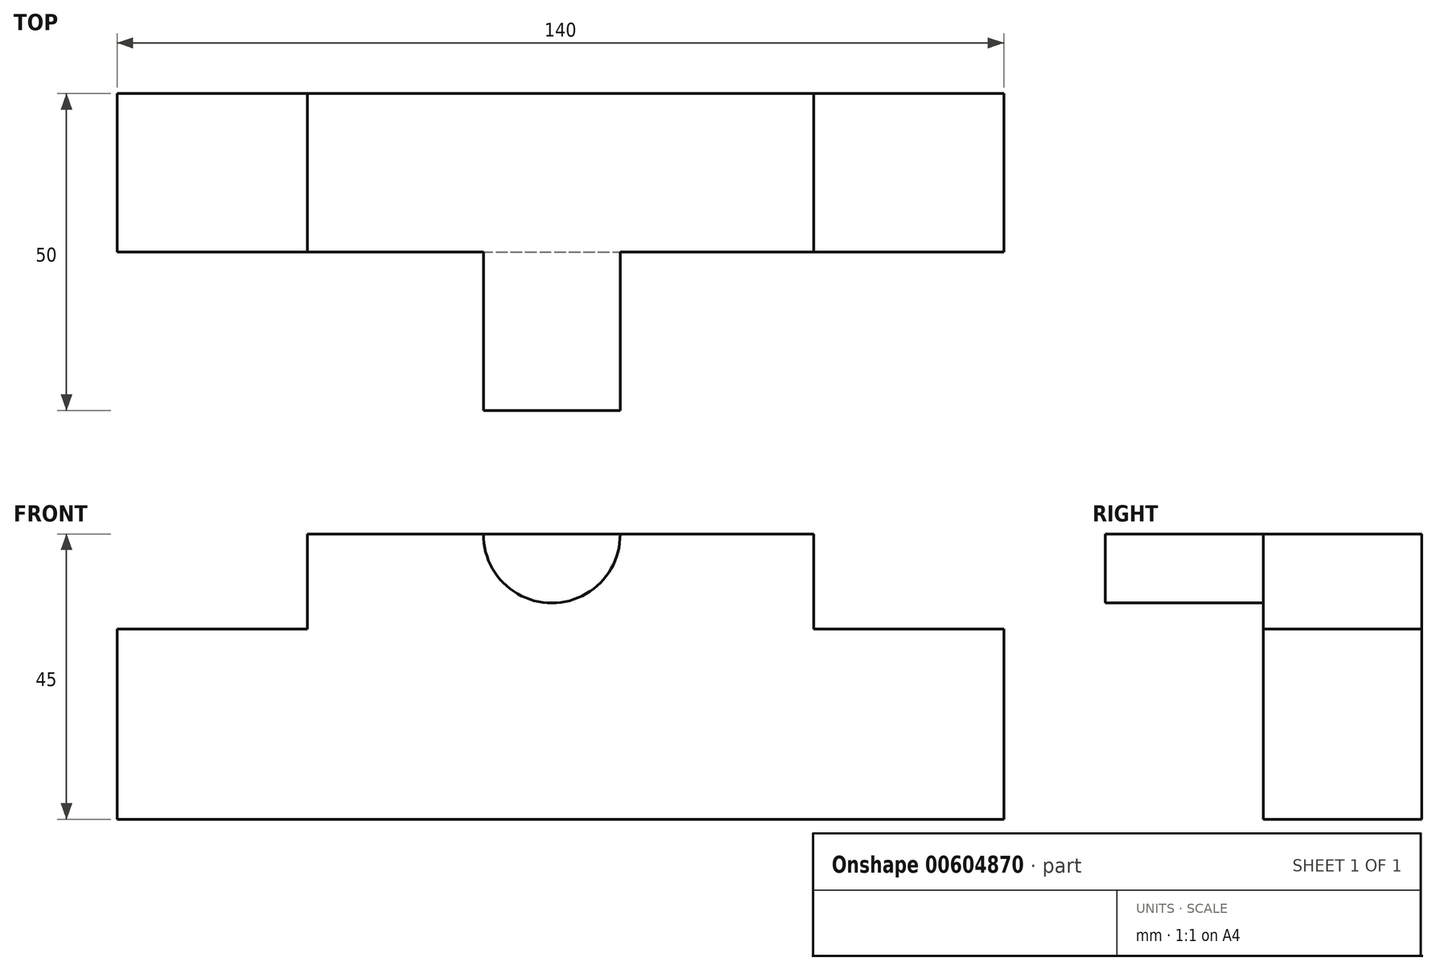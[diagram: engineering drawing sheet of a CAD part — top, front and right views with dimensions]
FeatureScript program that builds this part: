
annotation { "Feature Type Name" : "Feature", "Feature Type Description" : "" }
export const myFeature = defineFeature(function(context is Context, id is Id, definition is map)
    precondition{}
    {
        {
            var Q0;
            Q0=qCreatedBy(makeId("Front.planeOp"),FACE);
            var sketch = newSketch(context, id + "F0", { "sketchPlane" : qUnion([Q0])});
            skLineSegment(sketch, "E0", {"start": v(-68.52, 0) * mm, "end": v(71.48, 0) * mm});
            skLineSegment(sketch, "E1", {"start": v(-68.52, 0) * mm, "end": v(-68.52, 30) * mm});
            skLineSegment(sketch, "E2", {"start": v(71.48, 0) * mm, "end": v(71.48, 30) * mm});
            skLineSegment(sketch, "E3", {"start": v(-68.52, 30) * mm, "end": v(-38.52, 30) * mm});
            skLineSegment(sketch, "E4", {"start": v(71.48, 30) * mm, "end": v(41.48, 30) * mm});
            skLineSegment(sketch, "E5", {"start": v(-38.52, 30) * mm, "end": v(-38.52, 45) * mm});
            skLineSegment(sketch, "E6", {"start": v(-38.52, 45) * mm, "end": v(41.48, 45) * mm});
            skLineSegment(sketch, "E7", {"start": v(41.48, 45) * mm, "end": v(41.48, 30) * mm});
            skSolve(sketch);
        }
        {
            var Q0;
            Q0=makeQuery(id+"F0.imprint","IMPRINT",FACE,{"disambiguationData":[TD([[makeQuery(id+"F0.imprint","IMPRINT",EDGE,{"derivedFrom":sQuery(id+"F0.wireOp",EDGE,"E0")}),1.0]])]});
            extrude(context, id + "F1", {"entities" : qUnion([Q0]), "depth" : 25 * mm, "offsetDistance" : 25 * mm});
        }
        {
            var Q0;
            Q0=makeQuery(id+"F1.opExtrude","CAP_FACE",FACE,{"disambiguationData":[OSD([sQuery(id+"F0.wireOp",EDGE,"E0"),sQuery(id+"F0.wireOp",EDGE,"E1"),sQuery(id+"F0.wireOp",EDGE,"E2"),sQuery(id+"F0.wireOp",EDGE,"E3"),sQuery(id+"F0.wireOp",EDGE,"E4"),sQuery(id+"F0.wireOp",EDGE,"E5"),sQuery(id+"F0.wireOp",EDGE,"E6"),sQuery(id+"F0.wireOp",EDGE,"E7")])],"isStart":false});
            var sketch = newSketch(context, id + "F2", { "sketchPlane" : qUnion([Q0])});
            skCircle(sketch, "E8", {"center": v(0.1, 44.9) * mm, "radius": 10.79 * mm});
            skSolve(sketch);
        }
        {
            var Q0;
            {var subQ0=sQuery(id+"F2.wireOp",EDGE,"E8");var subQ1=makeQuery(id+"F1.opExtrude","CAP_EDGE",EDGE,{"disambiguationData":[OSD([sQuery(id+"F0.wireOp",EDGE,"E6")])],"isStart":false});var subQ2=makeQuery(id+"F2.imprint","INTERSECT",VERTEX,{"disambiguationData":[OD(0.0)],"derivedFrom":[subQ1,subQ0]});Q0=makeQuery(id+"F2.imprint","IMPRINT",FACE,{"disambiguationData":[TD([[makeQuery(id+"F2.imprint","IMPRINT",EDGE,{"disambiguationData":[TD([[subQ2,-1.0]])],"derivedFrom":subQ0}),1.0]])]});}
            extrude(context, id + "F3", {"entities" : qUnion([Q0]), "operationType" : NewBodyOperationType.ADD, "depth" : 25 * mm, "offsetDistance" : 25 * mm});
        }
    });
